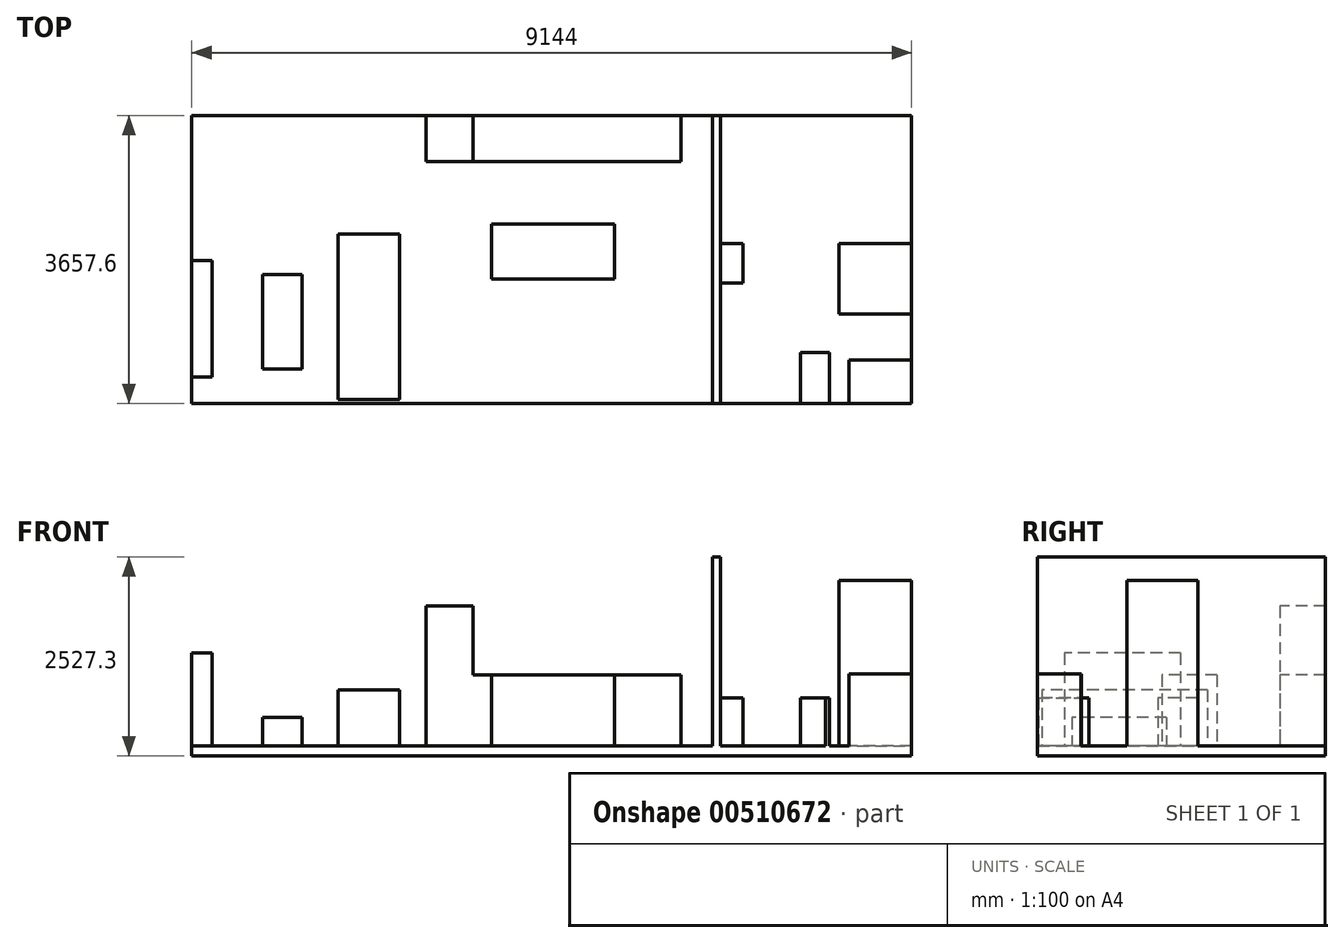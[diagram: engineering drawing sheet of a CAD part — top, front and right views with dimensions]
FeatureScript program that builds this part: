
annotation { "Feature Type Name" : "Feature", "Feature Type Description" : "" }
export const myFeature = defineFeature(function(context is Context, id is Id, definition is map)
    precondition{}
    {
        {
            var Q0;
            Q0=qCreatedBy(makeId("Top.planeOp"),FACE);
            var sketch = newSketch(context, id + "F0", { "sketchPlane" : qUnion([Q0])});
            skLineSegment(sketch, "E0.bottom", {"start": v(0, 0) * mm, "end": v(9144, 0) * mm});
            skLineSegment(sketch, "E0.top", {"start": v(0, -3657.6) * mm, "end": v(9144, -3657.6) * mm});
            skLineSegment(sketch, "E0.left", {"start": v(0, 0) * mm, "end": v(0, -3657.6) * mm});
            skLineSegment(sketch, "E0.right", {"start": v(9144, 0) * mm, "end": v(9144, -3657.6) * mm});
            skSolve(sketch);
        }
        {
            var Q0;
            Q0 = qSketchRegion(id + "F0", true);
            extrude(context, id + "F1", {"entities" : qUnion([Q0]), "oppositeDirection" : true, "depth" : 127 * mm, "offsetDistance" : 30.48 * mm});
        }
        {
            var Q0;
            Q0=makeQuery(id+"F1.opExtrude","CAP_FACE",FACE,{"disambiguationData":[OSD([sQuery(id+"F0.wireOp",EDGE,"E0.bottom"),sQuery(id+"F0.wireOp",EDGE,"E0.top"),sQuery(id+"F0.wireOp",EDGE,"E0.left"),sQuery(id+"F0.wireOp",EDGE,"E0.right")])],"isStart":true});
            var sketch = newSketch(context, id + "F2", { "sketchPlane" : qUnion([Q0])});
            skLineSegment(sketch, "E1", {"start": v(9144, -3657.6) * mm, "end": v(6705.6, -3657.6) * mm, "construction": true});
            skLineSegment(sketch, "E2", {"start": v(6705.6, -3657.6) * mm, "end": v(6705.6, -1615.44) * mm, "construction": true});
            skLineSegment(sketch, "E3", {"start": v(6705.6, -1615.44) * mm, "end": v(9144, -1615.44) * mm, "construction": true});
            skLineSegment(sketch, "E4", {"start": v(9144, -1615.44) * mm, "end": v(6705.6, -1615.44) * mm, "construction": true});
            skLineSegment(sketch, "E5", {"start": v(6705.6, 0) * mm, "end": v(6705.6, -1615.44) * mm, "construction": true});
            skLineSegment(sketch, "E6", {"start": v(2279.66, 0) * mm, "end": v(2279.66, -762) * mm, "construction": true});
            skLineSegment(sketch, "E7", {"start": v(2279.66, -762) * mm, "end": v(0, -762) * mm, "construction": true});
            skLineSegment(sketch, "E8", {"start": v(1858.95, -1503.68) * mm, "end": v(2638.73, -1503.68) * mm, "construction": true});
            skLineSegment(sketch, "E9", {"start": v(2638.73, -1503.68) * mm, "end": v(2638.73, -3606.8) * mm, "construction": true});
            skLineSegment(sketch, "E10", {"start": v(2638.73, -3606.8) * mm, "end": v(1858.95, -3606.8) * mm, "construction": true});
            skLineSegment(sketch, "E11", {"start": v(1858.95, -3606.8) * mm, "end": v(1858.95, -1503.68) * mm, "construction": true});
            skLineSegment(sketch, "E12", {"start": v(1401.75, -2015.77) * mm, "end": v(901.37, -2015.77) * mm, "construction": true});
            skLineSegment(sketch, "E13", {"start": v(901.37, -2015.77) * mm, "end": v(901.37, -3214.65) * mm, "construction": true});
            skLineSegment(sketch, "E14", {"start": v(901.37, -3214.65) * mm, "end": v(1401.75, -3214.65) * mm, "construction": true});
            skLineSegment(sketch, "E15", {"start": v(1401.75, -3214.65) * mm, "end": v(1401.75, -2015.77) * mm, "construction": true});
            skLineSegment(sketch, "E16", {"start": v(0, -1861.82) * mm, "end": v(276.86, -1861.82) * mm, "construction": true});
            skLineSegment(sketch, "E17", {"start": v(276.86, -1861.82) * mm, "end": v(276.86, -3302) * mm, "construction": true});
            skLineSegment(sketch, "E18", {"start": v(276.86, -3302) * mm, "end": v(0, -3302) * mm, "construction": true});
            skLineSegment(sketch, "E19", {"start": v(2943.9, 0) * mm, "end": v(2943.9, -599.44) * mm, "construction": true});
            skLineSegment(sketch, "E20", {"start": v(2943.9, -599.44) * mm, "end": v(6220.5, -599.44) * mm, "construction": true});
            skLineSegment(sketch, "E21", {"start": v(6220.5, -599.44) * mm, "end": v(6220.5, 0) * mm, "construction": true});
            skLineSegment(sketch, "E22", {"start": v(3810, -1381.76) * mm, "end": v(3810, -2082.8) * mm, "construction": true});
            skLineSegment(sketch, "E23", {"start": v(3810, -2082.8) * mm, "end": v(5359.4, -2082.8) * mm, "construction": true});
            skLineSegment(sketch, "E24", {"start": v(5359.4, -2082.8) * mm, "end": v(5359.4, -1381.76) * mm, "construction": true});
            skLineSegment(sketch, "E25", {"start": v(5359.4, -1381.76) * mm, "end": v(3810, -1381.76) * mm, "construction": true});
            skLineSegment(sketch, "E26", {"start": v(9144, 0) * mm, "end": v(9144, 0) * mm});
            skLineSegment(sketch, "E27", {"start": v(9144, -1615.44) * mm, "end": v(9144, -1361.44) * mm, "construction": true});
            skLineSegment(sketch, "E28", {"start": v(9144, -1361.44) * mm, "end": v(7741.92, -1361.44) * mm, "construction": true});
            skLineSegment(sketch, "E29", {"start": v(7741.92, -1361.44) * mm, "end": v(7741.92, -1615.44) * mm, "construction": true});
            skLineSegment(sketch, "E30", {"start": v(8229.6, -1615.44) * mm, "end": v(8229.6, -2509.52) * mm, "construction": true});
            skLineSegment(sketch, "E31", {"start": v(8229.6, -2509.52) * mm, "end": v(9144, -2509.52) * mm, "construction": true});
            skLineSegment(sketch, "E32", {"start": v(8341.36, -3657.6) * mm, "end": v(8341.36, -3111.5) * mm, "construction": true});
            skLineSegment(sketch, "E33", {"start": v(8341.36, -3111.5) * mm, "end": v(9144, -3111.5) * mm, "construction": true});
            skLineSegment(sketch, "E34", {"start": v(7741.92, -3657.6) * mm, "end": v(7741.92, -3007.36) * mm, "construction": true});
            skLineSegment(sketch, "E35", {"start": v(7741.92, -3007.36) * mm, "end": v(8092.44, -3007.36) * mm, "construction": true});
            skLineSegment(sketch, "E36", {"start": v(8092.44, -3007.36) * mm, "end": v(8092.44, -3657.6) * mm, "construction": true});
            skLineSegment(sketch, "E37", {"start": v(6705.6, -2123.44) * mm, "end": v(7010.4, -2123.44) * mm, "construction": true});
            skLineSegment(sketch, "E38", {"start": v(7010.4, -2123.44) * mm, "end": v(7010.4, -1615.44) * mm, "construction": true});
            skLineSegment(sketch, "E39", {"start": v(7313, -1615.44) * mm, "end": v(7313, -1717.04) * mm, "construction": true});
            skLineSegment(sketch, "E40", {"start": v(7313, -1717.04) * mm, "end": v(7912.45, -1717.04) * mm, "construction": true});
            skLineSegment(sketch, "E41", {"start": v(7912.45, -1717.04) * mm, "end": v(7912.45, -1615.44) * mm, "construction": true});
            skLineSegment(sketch, "E42", {"start": v(8549.64, 0) * mm, "end": v(9144, 0) * mm, "construction": true});
            skLineSegment(sketch, "E43", {"start": v(9144, -579.12) * mm, "end": v(8549.64, -579.12) * mm, "construction": true});
            skLineSegment(sketch, "E44", {"start": v(8549.64, -579.12) * mm, "end": v(8549.64, 0) * mm, "construction": true});
            skLineSegment(sketch, "E45", {"start": v(8430.05, 0) * mm, "end": v(8430.05, -579.12) * mm, "construction": true});
            skLineSegment(sketch, "E46", {"start": v(8430.05, -579.12) * mm, "end": v(7835.7, -579.12) * mm, "construction": true});
            skLineSegment(sketch, "E47", {"start": v(7835.7, -579.12) * mm, "end": v(7835.7, 0) * mm, "construction": true});
            skLineSegment(sketch, "E48", {"start": v(7772.4, 0) * mm, "end": v(7772.4, -480.06) * mm, "construction": true});
            skLineSegment(sketch, "E49", {"start": v(7772.4, -480.06) * mm, "end": v(7251.7, -480.06) * mm, "construction": true});
            skLineSegment(sketch, "E50", {"start": v(7251.7, -480.06) * mm, "end": v(7251.7, 0) * mm, "construction": true});
            skLineSegment(sketch, "E51", {"start": v(3543.33, -599.44) * mm, "end": v(3543.33, 0) * mm, "construction": true});
            skSolve(sketch);
        }
        {
            var Q0;
            Q0=makeQuery(id+"F2.imprint","IMPRINT",FACE,{"disambiguationData":[TD([[makeQuery(id+"F2.imprint","IMPRINT",EDGE,{"derivedFrom":makeQuery(id+"F1.opExtrude","CAP_EDGE",EDGE,{"disambiguationData":[OSD([sQuery(id+"F0.wireOp",EDGE,"E0.bottom")])],"isStart":true})}),-1.0]])]});
            var sketch = newSketch(context, id + "F3", { "sketchPlane" : qUnion([Q0])});
            skLineSegment(sketch, "E52", {"start": v(2639.57, -1502.01) * mm, "end": v(2639.57, -3605.25) * mm});
            skLineSegment(sketch, "E53", {"start": v(2639.57, -3605.25) * mm, "end": v(1859.55, -3605.25) * mm});
            skLineSegment(sketch, "E54", {"start": v(1859.55, -3605.25) * mm, "end": v(1859.55, -1502.01) * mm});
            skLineSegment(sketch, "E55", {"start": v(1859.55, -1502.01) * mm, "end": v(2639.57, -1502.01) * mm});
            skLineSegment(sketch, "E56", {"start": v(1401.12, -2019.33) * mm, "end": v(1401.12, -3222.14) * mm});
            skLineSegment(sketch, "E57", {"start": v(1401.12, -3222.14) * mm, "end": v(900.79, -3222.14) * mm});
            skLineSegment(sketch, "E58", {"start": v(900.79, -3222.14) * mm, "end": v(900.79, -2019.33) * mm});
            skLineSegment(sketch, "E59", {"start": v(900.79, -2019.33) * mm, "end": v(1401.12, -2019.33) * mm});
            skLineSegment(sketch, "E60", {"start": v(0, -1843.34) * mm, "end": v(256.63, -1843.34) * mm});
            skLineSegment(sketch, "E61", {"start": v(256.63, -1843.34) * mm, "end": v(256.63, -3320.14) * mm});
            skLineSegment(sketch, "E62", {"start": v(256.63, -3320.14) * mm, "end": v(0, -3320.14) * mm});
            skLineSegment(sketch, "E63", {"start": v(0, -3320.14) * mm, "end": v(0, -1843.34) * mm});
            skLineSegment(sketch, "E64", {"start": v(2263.05, 0) * mm, "end": v(2263.05, -756.99) * mm});
            skLineSegment(sketch, "E65", {"start": v(2263.05, -756.99) * mm, "end": v(0, -756.99) * mm});
            skLineSegment(sketch, "E66", {"start": v(0, -756.99) * mm, "end": v(0, 0) * mm});
            skLineSegment(sketch, "E67", {"start": v(0, 0) * mm, "end": v(2263.05, 0) * mm});
            skLineSegment(sketch, "E68", {"start": v(3572.7, 0) * mm, "end": v(3572.7, -582.62) * mm});
            skLineSegment(sketch, "E69", {"start": v(3572.7, -582.62) * mm, "end": v(2974.9, -582.62) * mm});
            skLineSegment(sketch, "E70", {"start": v(2974.9, -582.62) * mm, "end": v(2974.9, 0) * mm});
            skLineSegment(sketch, "E71", {"start": v(2974.9, 0) * mm, "end": v(3572.7, 0) * mm});
            skLineSegment(sketch, "E72", {"start": v(3572.7, -582.62) * mm, "end": v(6213.04, -582.62) * mm});
            skLineSegment(sketch, "E73", {"start": v(6213.04, -582.62) * mm, "end": v(6213.04, 0) * mm});
            skLineSegment(sketch, "E74", {"start": v(6213.04, 0) * mm, "end": v(3572.7, 0) * mm});
            skLineSegment(sketch, "E75", {"start": v(3805.19, -1379.7) * mm, "end": v(3805.19, -2077.15) * mm});
            skLineSegment(sketch, "E76", {"start": v(3805.19, -2077.15) * mm, "end": v(5366.93, -2077.15) * mm});
            skLineSegment(sketch, "E77", {"start": v(5366.93, -2077.15) * mm, "end": v(5366.93, -1379.7) * mm});
            skLineSegment(sketch, "E78", {"start": v(5366.93, -1379.7) * mm, "end": v(3805.19, -1379.7) * mm});
            skLineSegment(sketch, "E79", {"start": v(6712.44, 0) * mm, "end": v(6712.44, -3156.07) * mm});
            skLineSegment(sketch, "E80", {"start": v(6712.44, -3156.07) * mm, "end": v(6712.44, -1578.04) * mm});
            skLineSegment(sketch, "E81", {"start": v(6712.44, -1623.73) * mm, "end": v(9148.92, -1623.73) * mm});
            skLineSegment(sketch, "E82", {"start": v(9148.92, -1623.73) * mm, "end": v(9148.92, -1353.66) * mm});
            skLineSegment(sketch, "E83", {"start": v(9148.92, -1353.66) * mm, "end": v(7734, -1353.66) * mm});
            skLineSegment(sketch, "E84", {"start": v(7734, -1353.66) * mm, "end": v(7734, -1623.73) * mm});
            skLineSegment(sketch, "E85", {"start": v(7775.1, 0) * mm, "end": v(7775.1, -467.13) * mm});
            skLineSegment(sketch, "E86", {"start": v(7775.1, -467.13) * mm, "end": v(7258.45, -467.13) * mm});
            skLineSegment(sketch, "E87", {"start": v(7258.45, -467.13) * mm, "end": v(7258.45, 0) * mm});
            skLineSegment(sketch, "E88", {"start": v(7258.45, 0) * mm, "end": v(7775.1, 0) * mm});
            skLineSegment(sketch, "E89", {"start": v(7775.1, 0) * mm, "end": v(7827.94, 0) * mm});
            skLineSegment(sketch, "E90", {"start": v(7827.94, 0) * mm, "end": v(7827.94, -572.8) * mm});
            skLineSegment(sketch, "E91", {"start": v(7827.94, -572.8) * mm, "end": v(8438.53, -572.8) * mm});
            skLineSegment(sketch, "E92", {"start": v(8438.53, -572.8) * mm, "end": v(8438.53, 0) * mm});
            skLineSegment(sketch, "E93", {"start": v(8438.53, 0) * mm, "end": v(7827.94, 0) * mm});
            skLineSegment(sketch, "E94", {"start": v(8561.82, 0) * mm, "end": v(8561.82, -578.68) * mm});
            skLineSegment(sketch, "E95", {"start": v(8561.82, -578.68) * mm, "end": v(9148.92, -578.68) * mm});
            skLineSegment(sketch, "E96", {"start": v(9148.92, -578.68) * mm, "end": v(9148.92, 0) * mm});
            skLineSegment(sketch, "E97", {"start": v(9148.92, 0) * mm, "end": v(8561.82, 0) * mm});
            skLineSegment(sketch, "E98", {"start": v(7000.86, -1623.73) * mm, "end": v(7000.86, -2129.35) * mm});
            skLineSegment(sketch, "E99", {"start": v(7000.86, -2129.35) * mm, "end": v(6712.44, -2129.35) * mm});
            skLineSegment(sketch, "E100", {"start": v(6712.44, -2129.35) * mm, "end": v(6712.44, -1623.73) * mm});
            skLineSegment(sketch, "E101", {"start": v(7315.05, -1623.73) * mm, "end": v(7315.05, -1745.34) * mm});
            skLineSegment(sketch, "E102", {"start": v(7315.05, -1745.34) * mm, "end": v(7915.5, -1745.34) * mm});
            skLineSegment(sketch, "E103", {"start": v(7915.5, -1745.34) * mm, "end": v(7915.5, -1623.73) * mm});
            skLineSegment(sketch, "E104", {"start": v(7915.5, -1623.73) * mm, "end": v(7877.94, -1623.73) * mm});
            skLineSegment(sketch, "E105", {"start": v(7877.94, -1623.73) * mm, "end": v(7877.94, -1713.8) * mm});
            skLineSegment(sketch, "E106", {"start": v(7877.94, -1713.8) * mm, "end": v(7355.17, -1713.8) * mm});
            skLineSegment(sketch, "E107", {"start": v(7355.17, -1713.8) * mm, "end": v(7355.17, -1623.73) * mm});
            skLineSegment(sketch, "E108", {"start": v(8221.5, -1623.73) * mm, "end": v(8221.5, -2520.48) * mm});
            skLineSegment(sketch, "E109", {"start": v(8221.5, -2520.48) * mm, "end": v(9150.09, -2520.48) * mm});
            skLineSegment(sketch, "E110", {"start": v(9150.09, -2520.48) * mm, "end": v(9148.92, -1623.73) * mm});
            skLineSegment(sketch, "E111", {"start": v(8098.97, -3658.74) * mm, "end": v(8098.97, -3006.96) * mm});
            skLineSegment(sketch, "E112", {"start": v(8098.97, -3006.96) * mm, "end": v(7733.64, -3006.96) * mm});
            skLineSegment(sketch, "E113", {"start": v(7733.64, -3006.96) * mm, "end": v(7733.64, -3650.43) * mm});
            skLineSegment(sketch, "E114", {"start": v(7733.64, -3650.43) * mm, "end": v(8098.97, -3658.74) * mm});
            skLineSegment(sketch, "E115", {"start": v(8348.05, -3102.44) * mm, "end": v(8348.05, -3658.74) * mm});
            skLineSegment(sketch, "E116", {"start": v(8348.05, -3658.74) * mm, "end": v(9148.92, -3658.74) * mm});
            skLineSegment(sketch, "E117", {"start": v(9148.92, -3658.74) * mm, "end": v(9148.92, -3106.6) * mm});
            skLineSegment(sketch, "E118", {"start": v(9148.92, -3106.6) * mm, "end": v(8348.05, -3102.44) * mm});
            skLineSegment(sketch, "E119", {"start": v(6712.44, -3156.07) * mm, "end": v(6712.44, -3658.74) * mm});
            skLineSegment(sketch, "E120", {"start": v(6712.44, -3658.74) * mm, "end": v(6614.9, -3658.74) * mm});
            skLineSegment(sketch, "E121", {"start": v(6614.9, -3658.74) * mm, "end": v(6614.9, 0) * mm});
            skLineSegment(sketch, "E122", {"start": v(6614.9, 0) * mm, "end": v(6712.44, 0) * mm});
            skSolve(sketch);
        }
        {
            var Q0;
            Q0=makeQuery(id+"F3.imprint","IMPRINT",FACE,{"disambiguationData":[TD([[makeQuery(id+"F3.imprint","IMPRINT",EDGE,{"derivedFrom":sQuery(id+"F3.wireOp",EDGE,"E52")}),-1.0]])]});
            extrude(context, id + "F4", {"entities" : qUnion([Q0]), "operationType" : NewBodyOperationType.ADD, "depth" : 711.2 * mm, "offsetDistance" : 25.4 * mm});
        }
        {
            var Q0;
            Q0=makeQuery(id+"F3.imprint","IMPRINT",FACE,{"disambiguationData":[TD([[makeQuery(id+"F3.imprint","IMPRINT",EDGE,{"derivedFrom":sQuery(id+"F3.wireOp",EDGE,"E56")}),-1.0]])]});
            extrude(context, id + "F5", {"entities" : qUnion([Q0]), "depth" : 360.68 * mm, "offsetDistance" : 25.4 * mm});
        }
        {
            var Q0;
            Q0=makeQuery(id+"F3.imprint","IMPRINT",FACE,{"disambiguationData":[TD([[makeQuery(id+"F3.imprint","IMPRINT",EDGE,{"derivedFrom":sQuery(id+"F3.wireOp",EDGE,"E60")}),-1.0]])]});
            extrude(context, id + "F6", {"entities" : qUnion([Q0]), "operationType" : NewBodyOperationType.ADD, "depth" : 1178.56 * mm, "offsetDistance" : 25.4 * mm});
        }
        {
            var Q0;
            Q0=makeQuery(id+"F3.imprint","IMPRINT",FACE,{"disambiguationData":[TD([[makeQuery(id+"F3.imprint","IMPRINT",EDGE,{"derivedFrom":sQuery(id+"F3.wireOp",EDGE,"E68")}),-1.0]])]});
            extrude(context, id + "F7", {"entities" : qUnion([Q0]), "operationType" : NewBodyOperationType.ADD, "depth" : 1778 * mm, "offsetDistance" : 25.4 * mm});
        }
        {
            var Q0;
            Q0=makeQuery(id+"F3.imprint","IMPRINT",FACE,{"disambiguationData":[TD([[makeQuery(id+"F3.imprint","IMPRINT",EDGE,{"derivedFrom":sQuery(id+"F3.wireOp",EDGE,"E68")}),1.0]])]});
            extrude(context, id + "F8", {"entities" : qUnion([Q0]), "operationType" : NewBodyOperationType.ADD, "depth" : 899.16 * mm, "offsetDistance" : 25.4 * mm});
        }
        {
            var Q0;
            Q0=makeQuery(id+"F3.imprint","IMPRINT",FACE,{"disambiguationData":[TD([[makeQuery(id+"F3.imprint","IMPRINT",EDGE,{"derivedFrom":sQuery(id+"F3.wireOp",EDGE,"E75")}),1.0]])]});
            extrude(context, id + "F9", {"entities" : qUnion([Q0]), "operationType" : NewBodyOperationType.ADD, "depth" : 899.16 * mm, "offsetDistance" : 25.4 * mm});
        }
        {
            var Q0;
            {var subQ2=sQuery(id+"F3.wireOp",EDGE,"E98");Q0=makeQuery(id+"F3.imprint","IMPRINT",FACE,{"disambiguationData":[TD([[makeQuery(id+"F3.imprint","IMPRINT",EDGE,{"derivedFrom":subQ2}),-1.0]])]});}
            extrude(context, id + "F10", {"entities" : qUnion([Q0]), "operationType" : NewBodyOperationType.ADD, "depth" : 609.6 * mm, "offsetDistance" : 25.4 * mm});
        }
        {
            var Q0;
            {var subQ4=sQuery(id+"F3.wireOp",EDGE,"E112");Q0=makeQuery(id+"F3.imprint","IMPRINT",FACE,{"disambiguationData":[TD([[makeQuery(id+"F3.imprint","IMPRINT",EDGE,{"derivedFrom":subQ4}),1.0]])]});}
            extrude(context, id + "F11", {"entities" : qUnion([Q0]), "operationType" : NewBodyOperationType.ADD, "depth" : 609.6 * mm, "offsetDistance" : 25.4 * mm});
        }
        {
            var Q0;
            {var subQ0=sQuery(id+"F3.wireOp",EDGE,"E108");Q0=makeQuery(id+"F3.imprint","IMPRINT",FACE,{"disambiguationData":[TD([[makeQuery(id+"F3.imprint","IMPRINT",EDGE,{"derivedFrom":subQ0}),1.0]])]});}
            extrude(context, id + "F12", {"entities" : qUnion([Q0]), "operationType" : NewBodyOperationType.ADD, "depth" : 2103.12 * mm, "offsetDistance" : 25.4 * mm});
        }
        {
            var Q0;
            {var subQ0=sQuery(id+"F3.wireOp",EDGE,"E118");var subQ1=sQuery(id+"F3.wireOp",EDGE,"E115");var subQ2=makeQuery(id+"F3.imprint","INTERSECT",VERTEX,{"derivedFrom":[subQ1,subQ0]});Q0=makeQuery(id+"F3.imprint","IMPRINT",FACE,{"disambiguationData":[TD([[makeQuery(id+"F3.imprint","IMPRINT",EDGE,{"disambiguationData":[TD([[subQ2,-1.0]])],"derivedFrom":subQ1}),1.0]])]});}
            extrude(context, id + "F13", {"entities" : qUnion([Q0]), "operationType" : NewBodyOperationType.ADD, "depth" : 914.4 * mm, "offsetDistance" : 25.4 * mm});
        }
        {
            var Q0;
            {var subQ2=sQuery(id+"F3.wireOp",EDGE,"E79");Q0=makeQuery(id+"F3.imprint","IMPRINT",FACE,{"disambiguationData":[TD([[makeQuery(id+"F3.imprint","IMPRINT",EDGE,{"derivedFrom":subQ2}),-1.0]])]});}
            extrude(context, id + "F14", {"entities" : qUnion([Q0]), "operationType" : NewBodyOperationType.ADD, "depth" : 2400.3 * mm, "offsetDistance" : 25.4 * mm});
        }
    });
